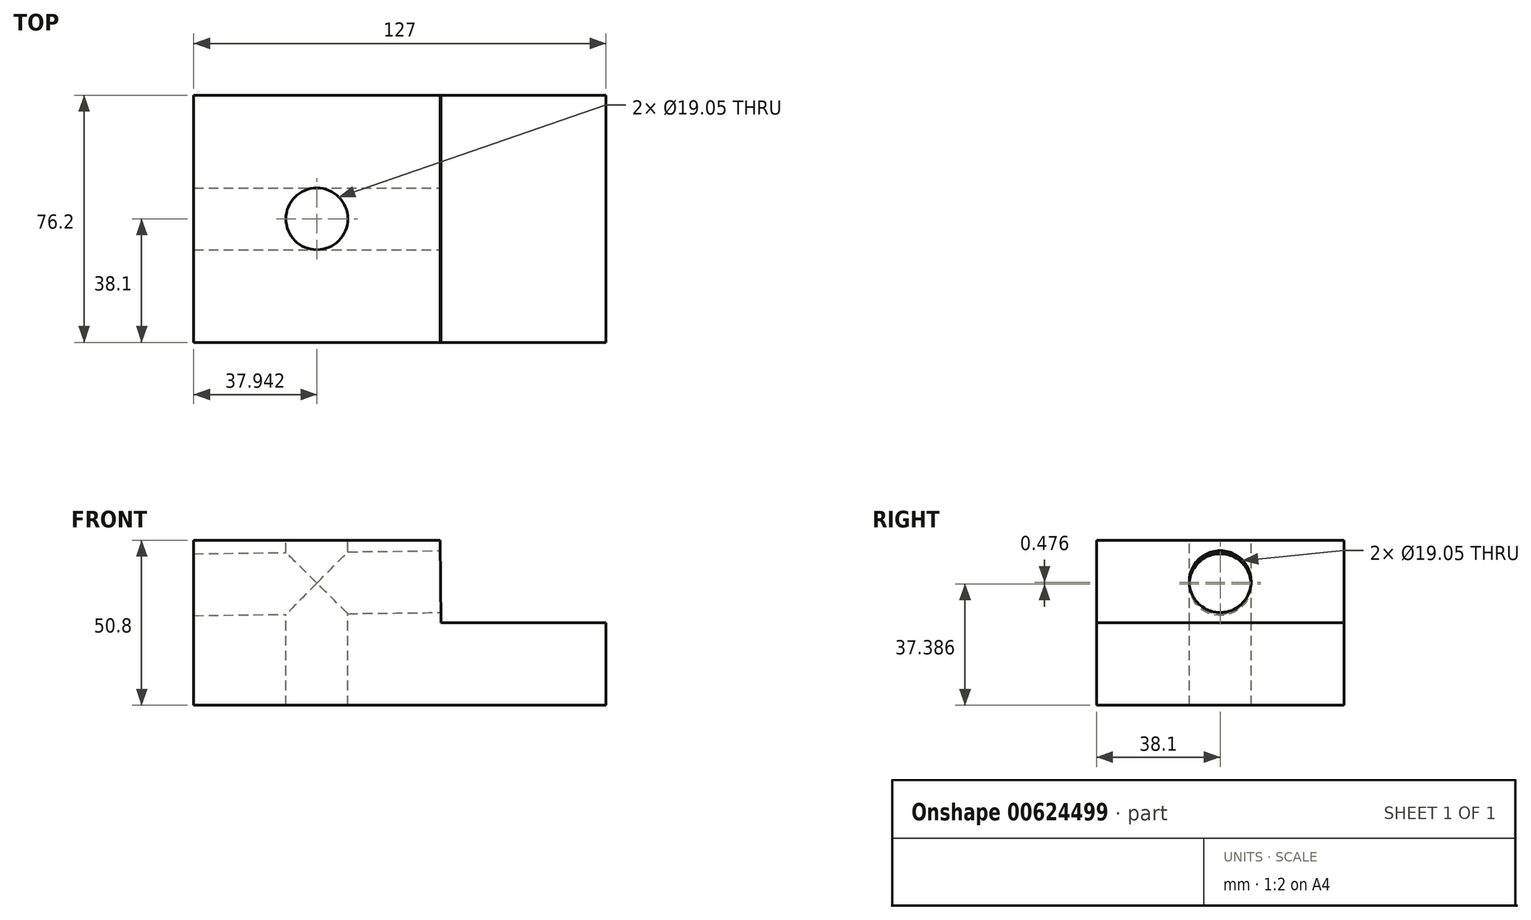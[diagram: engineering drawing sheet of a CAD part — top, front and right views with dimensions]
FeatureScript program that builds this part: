
annotation { "Feature Type Name" : "Feature", "Feature Type Description" : "" }
export const myFeature = defineFeature(function(context is Context, id is Id, definition is map)
    precondition{}
    {
        {
            var Q0;
            Q0=qCreatedBy(makeId("Front.planeOp"),FACE);
            var sketch = newSketch(context, id + "F0", { "sketchPlane" : qUnion([Q0])});
            skLineSegment(sketch, "E0.bottom", {"start": v(-31.79, -31.46) * mm, "end": v(95.21, -31.46) * mm});
            skLineSegment(sketch, "E0.top", {"start": v(-31.79, 19.34) * mm, "end": v(95.21, 19.34) * mm});
            skLineSegment(sketch, "E0.left", {"start": v(-31.79, -31.46) * mm, "end": v(-31.79, 19.34) * mm});
            skLineSegment(sketch, "E0.right", {"start": v(95.21, -31.46) * mm, "end": v(95.21, 19.34) * mm});
            skLineSegment(sketch, "E1", {"start": v(44.1, 19.34) * mm, "end": v(44.41, -6.06) * mm});
            skLineSegment(sketch, "E2", {"start": v(44.41, -6.06) * mm, "end": v(95.21, -6.06) * mm});
            skSolve(sketch);
        }
        {
            var Q0;
            {var subQ1=sQuery(id+"F0.wireOp",EDGE,"E0.bottom");Q0=makeQuery(id+"F0.imprint","IMPRINT",FACE,{"disambiguationData":[TD([[makeQuery(id+"F0.imprint","IMPRINT",EDGE,{"derivedFrom":subQ1}),1.0]])]});}
            extrude(context, id + "F1", {"entities" : qUnion([Q0]), "depth" : 76.2 * mm, "offsetDistance" : 25.4 * mm});
        }
        {
            var Q0;
            Q0=makeQuery(id+"F1.opExtrude","SWEPT_FACE",FACE,{"disambiguationData":[OSD([sQuery(id+"F0.wireOp",EDGE,"E1")])]});
            var sketch = newSketch(context, id + "F2", { "sketchPlane" : qUnion([Q0])});
            skPoint(sketch, "E3", {"position": v(-38.1, 18.78) * mm});
            skPoint(sketch, "E4", {"position": v(-76.2, 6.08) * mm});
            skPoint(sketch, "E5", {"position": v(-38.1, 6.08) * mm});
            skSolve(sketch);
        }
        {
            var Q0;
            Q0=sQuery(id+"F2.wireOp",VERTEX,"E5");
            var Q1;
            Q1=makeQuery(id+"F1.opExtrude","SWEPT_BODY",BODY,{"disambiguationData":[OSD([sQuery(id+"F0.wireOp",EDGE,"E0.bottom"),sQuery(id+"F0.wireOp",EDGE,"E0.top"),sQuery(id+"F0.wireOp",EDGE,"E0.left"),sQuery(id+"F0.wireOp",EDGE,"E0.right"),sQuery(id+"F0.wireOp",EDGE,"E1"),sQuery(id+"F0.wireOp",EDGE,"E2")])]});
            hole(context, id + "F3", {"style" : HoleStyle.SIMPLE, "endStyle" : HoleEndStyle.THROUGH, "holeDiameter" : 19.05 * mm, "majorDiameter" : 6.35 * mm, "isTappedThrough" : true, "tappedDepth" : 12.7 * mm, "tapClearance" : 3, "locations" : qUnion([Q0]), "scope" : qUnion([Q1])});
        }
        {
            var Q0;
            Q0=makeQuery(id+"F1.opExtrude","SWEPT_FACE",FACE,{"disambiguationData":[OSD([sQuery(id+"F0.wireOp",EDGE,"E0.top")])]});
            var sketch = newSketch(context, id + "F4", { "sketchPlane" : qUnion([Q0])});
            skPoint(sketch, "E6", {"position": v(-31.79, -38.1) * mm});
            skPoint(sketch, "E7", {"position": v(6.15, -76.2) * mm});
            skPoint(sketch, "E8", {"position": v(6.15, -38.1) * mm});
            skSolve(sketch);
        }
        {
            var Q0;
            Q0=sQuery(id+"F4.wireOp",VERTEX,"E8");
            var Q1;
            Q1=makeQuery(id+"F1.opExtrude","SWEPT_BODY",BODY,{"disambiguationData":[OSD([sQuery(id+"F0.wireOp",EDGE,"E0.bottom"),sQuery(id+"F0.wireOp",EDGE,"E0.top"),sQuery(id+"F0.wireOp",EDGE,"E0.left"),sQuery(id+"F0.wireOp",EDGE,"E0.right"),sQuery(id+"F0.wireOp",EDGE,"E1"),sQuery(id+"F0.wireOp",EDGE,"E2")])]});
            hole(context, id + "F5", {"style" : HoleStyle.SIMPLE, "endStyle" : HoleEndStyle.THROUGH, "holeDiameter" : 19.05 * mm, "majorDiameter" : 6.35 * mm, "isTappedThrough" : true, "tappedDepth" : 12.7 * mm, "tapClearance" : 3, "locations" : qUnion([Q0]), "scope" : qUnion([Q1])});
        }
    });
